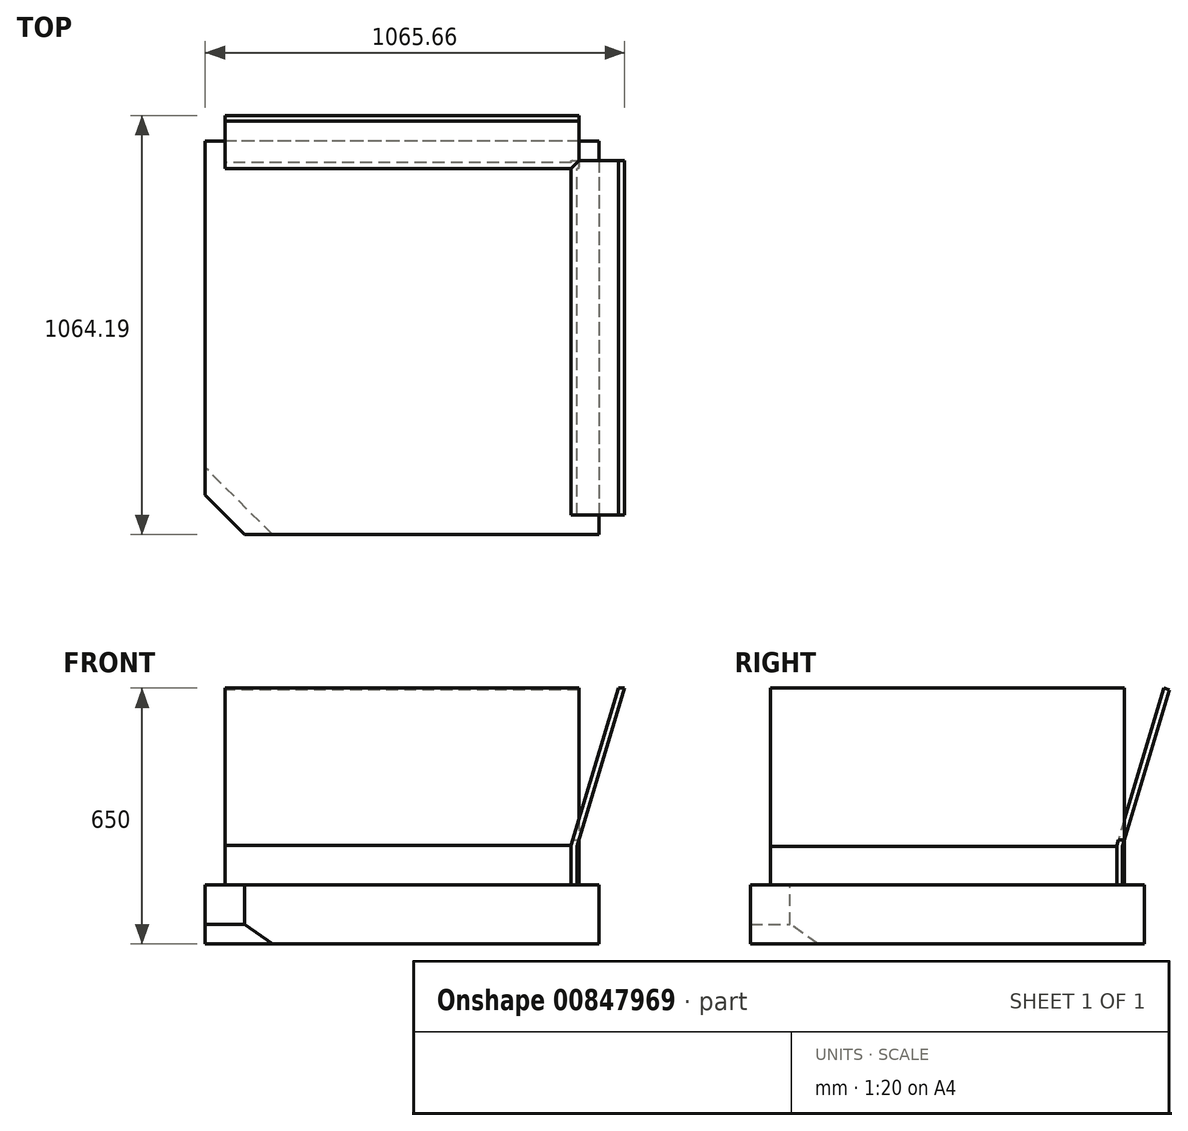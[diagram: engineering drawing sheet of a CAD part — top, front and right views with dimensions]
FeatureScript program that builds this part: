
annotation { "Feature Type Name" : "Feature", "Feature Type Description" : "" }
export const myFeature = defineFeature(function(context is Context, id is Id, definition is map)
    precondition{}
    {
        {
            var Q0;
            Q0=qCreatedBy(makeId("Right.planeOp"),FACE);
            var sketch = newSketch(context, id + "F0", { "sketchPlane" : qUnion([Q0])});
            skLineSegment(sketch, "E0.bottom", {"start": v(500, 75) * mm, "end": v(-500, 75) * mm});
            skLineSegment(sketch, "E0.top", {"start": v(500, -75) * mm, "end": v(-500, -75) * mm});
            skLineSegment(sketch, "E0.left", {"start": v(500, 75) * mm, "end": v(500, -75) * mm});
            skLineSegment(sketch, "E0.right", {"start": v(-500, 75) * mm, "end": v(-500, -75) * mm});
            skPoint(sketch, "E0.middle", {"position": v(0, 0) * mm});
            skSolve(sketch);
        }
        {
            var Q0;
            Q0=makeQuery(id+"F0.imprint","IMPRINT",FACE,{"disambiguationData":[TD([[makeQuery(id+"F0.imprint","IMPRINT",EDGE,{"derivedFrom":sQuery(id+"F0.wireOp",EDGE,"E0.bottom")}),1.0]])]});
            extrude(context, id + "F1", {"entities" : qUnion([Q0]), "endBound" : BoundingType.SYMMETRIC, "depth" : 1000 * mm, "offsetDistance" : 25 * mm});
        }
        {
            var Q0;
            Q0=qCreatedBy(makeId("Right.planeOp"),FACE);
            var sketch = newSketch(context, id + "F2", { "sketchPlane" : qUnion([Q0])});
            skLineSegment(sketch, "E1", {"start": v(430, 75) * mm, "end": v(430, 175) * mm});
            skLineSegment(sketch, "E2", {"start": v(430, 175) * mm, "end": v(550, 575) * mm});
            skLineSegment(sketch, "E3.0", {"start": v(445, 172.8) * mm, "end": v(564.2, 570.1) * mm});
            skLineSegment(sketch, "E3.1", {"start": v(445, 75) * mm, "end": v(445, 172.8) * mm});
            skLineSegment(sketch, "E4", {"start": v(430, 75) * mm, "end": v(445, 75) * mm});
            skLineSegment(sketch, "E5", {"start": v(550, 575) * mm, "end": v(564.2, 570.1) * mm});
            skSolve(sketch);
        }
        {
            var Q0;
            Q0=makeQuery(id+"F2.imprint","IMPRINT",FACE,{"disambiguationData":[TD([[makeQuery(id+"F2.imprint","IMPRINT",EDGE,{"derivedFrom":sQuery(id+"F2.wireOp",EDGE,"E1")}),-1.0]])]});
            extrude(context, id + "F3", {"entities" : qUnion([Q0]), "operationType" : NewBodyOperationType.ADD, "endBound" : BoundingType.SYMMETRIC, "depth" : 900 * mm, "offsetDistance" : 25 * mm});
        }
        {
            var Q0;
            Q0=qCreatedBy(makeId("Front.planeOp"),FACE);
            var sketch = newSketch(context, id + "F4", { "sketchPlane" : qUnion([Q0])});
            skLineSegment(sketch, "E6", {"start": v(430, 75) * mm, "end": v(430, 175) * mm});
            skLineSegment(sketch, "E7", {"start": v(430, 175) * mm, "end": v(550, 575) * mm});
            skLineSegment(sketch, "E8.0", {"start": v(445, 172.8) * mm, "end": v(565.66, 575) * mm});
            skLineSegment(sketch, "E8.1", {"start": v(445, 75) * mm, "end": v(445, 172.8) * mm});
            skLineSegment(sketch, "E9", {"start": v(430, 75) * mm, "end": v(445, 75) * mm});
            skLineSegment(sketch, "E10", {"start": v(550, 575) * mm, "end": v(565.66, 575) * mm});
            skSolve(sketch);
        }
        {
            var Q0;
            Q0 = qSketchRegion(id + "F4", true);
            extrude(context, id + "F5", {"entities" : qUnion([Q0]), "operationType" : NewBodyOperationType.ADD, "endBound" : BoundingType.SYMMETRIC, "depth" : 900 * mm, "offsetDistance" : 25 * mm});
        }
        {
            var Q0;
            Q0=makeQuery(id+"F1.opExtrude","CAP_EDGE",EDGE,{"disambiguationData":[OSD([sQuery(id+"F0.wireOp",EDGE,"E0.right")])],"isStart":true});
            chamfer(context, id + "F6", {"entities" : qUnion([Q0]), "width" : 100 * mm, "tangentPropagation" : true});
        }
        {
            var Q0;
            Q0=makeQuery(id+"F6.opChamfer","BLEND_EDGE",EDGE,{"blendedFrom":[makeQuery(id+"F1.opExtrude","CAP_EDGE",EDGE,{"disambiguationData":[OSD([sQuery(id+"F0.wireOp",EDGE,"E0.right")])],"isStart":true}),makeQuery(id+"F1.opExtrude","SWEPT_FACE",FACE,{"disambiguationData":[OSD([sQuery(id+"F0.wireOp",EDGE,"E0.top")])]})],"blendedInto":[makeQuery(id+"F1.opExtrude","SWEPT_FACE",FACE,{"disambiguationData":[OSD([sQuery(id+"F0.wireOp",EDGE,"E0.top")])]})]});
            chamfer(context, id + "F7", {"entities" : qUnion([Q0]), "width" : 50 * mm, "tangentPropagation" : true});
        }
    });
